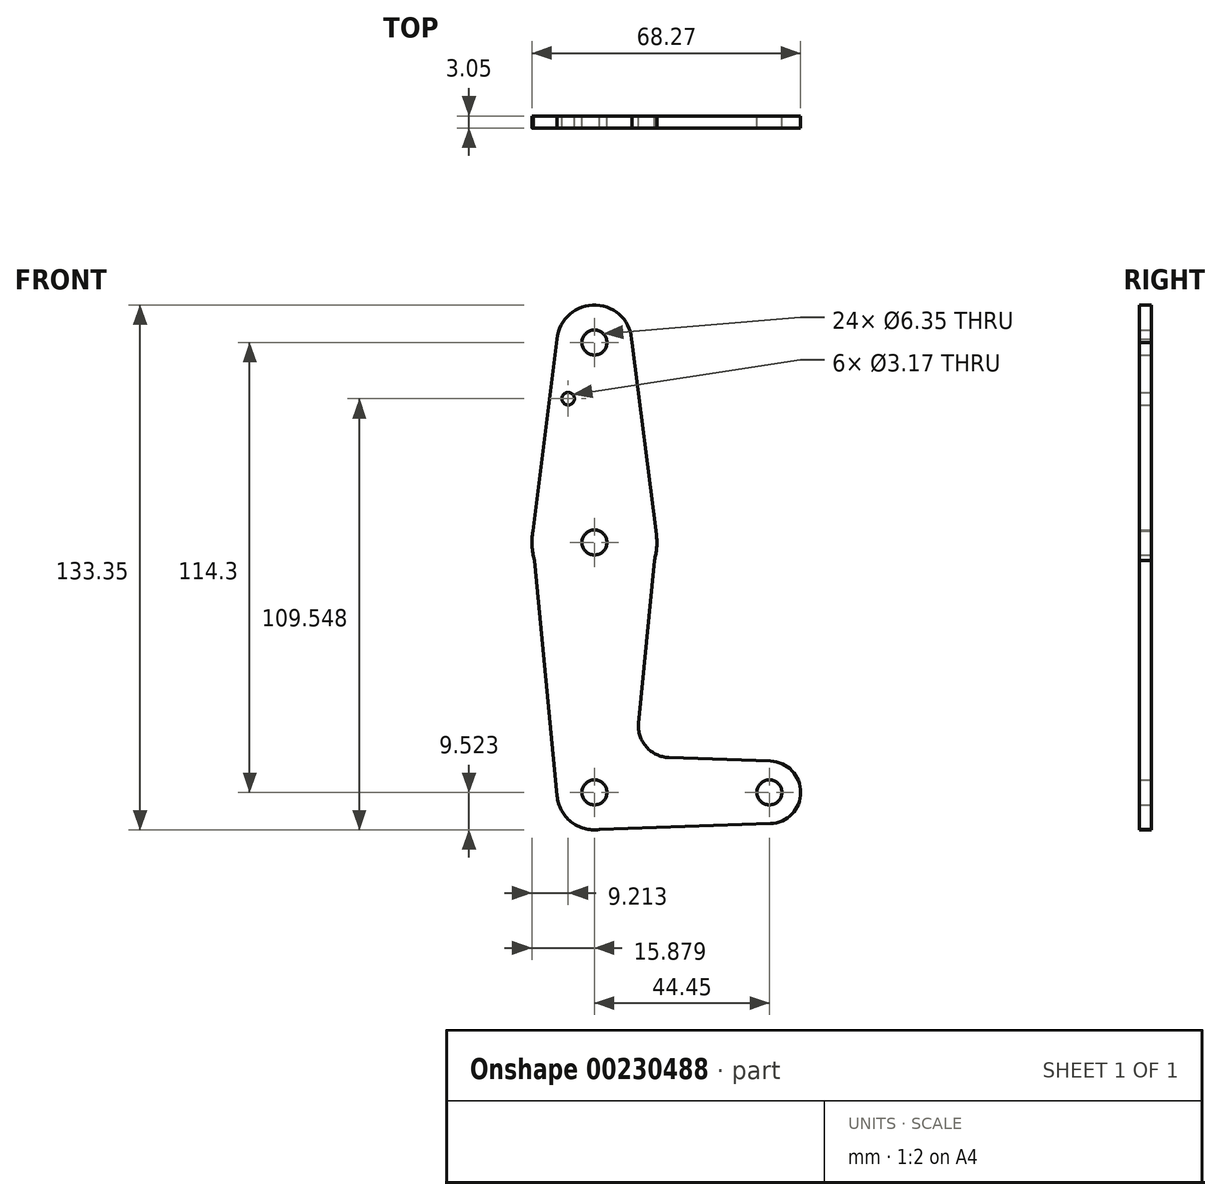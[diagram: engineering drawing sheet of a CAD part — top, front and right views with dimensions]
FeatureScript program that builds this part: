
annotation { "Feature Type Name" : "Feature", "Feature Type Description" : "" }
export const myFeature = defineFeature(function(context is Context, id is Id, definition is map)
    precondition{}
    {
        {
            var Q0;
            Q0=qCreatedBy(makeId("Front.planeOp"),FACE);
            var sketch = newSketch(context, id + "F0", { "sketchPlane" : qUnion([Q0])});
            skLineSegment(sketch, "E0", {"start": v(-22.85, 55.33) * mm, "end": v(-22.85, -58.97) * mm, "construction": true});
            skLineSegment(sketch, "E1", {"start": v(-22.85, -58.97) * mm, "end": v(21.6, -58.97) * mm, "construction": true});
            skCircle(sketch, "E2", {"center": v(-22.85, 55.33) * mm, "radius": 9.53 * mm});
            skCircle(sketch, "E3", {"center": v(-22.85, 4.53) * mm, "radius": 15.88 * mm});
            skCircle(sketch, "E4", {"center": v(-22.85, -58.97) * mm, "radius": 9.53 * mm});
            skCircle(sketch, "E5", {"center": v(21.6, -58.97) * mm, "radius": 7.94 * mm});
            skLineSegment(sketch, "E6", {"start": v(-32.33, 56.22) * mm, "end": v(-38.46, 7.42) * mm});
            skLineSegment(sketch, "E7", {"start": v(-3.98, -50.11) * mm, "end": v(21.88, -51.03) * mm});
            skLineSegment(sketch, "E8", {"start": v(-23.43, -68.47) * mm, "end": v(21.87, -66.9) * mm});
            skLineSegment(sketch, "E9", {"start": v(-7.64, 0) * mm, "end": v(-11.6, -41.41) * mm});
            skCircle(sketch, "E10", {"center": v(-22.85, 55.33) * mm, "radius": 3.18 * mm});
            skCircle(sketch, "E11", {"center": v(-22.85, 4.53) * mm, "radius": 3.18 * mm});
            skCircle(sketch, "E12", {"center": v(-22.85, -58.97) * mm, "radius": 3.18 * mm});
            skCircle(sketch, "E13", {"center": v(21.6, -58.97) * mm, "radius": 3.18 * mm});
            skCircle(sketch, "E14", {"center": v(-29.52, 41.06) * mm, "radius": 1.59 * mm});
            skArc(sketch, "E15.filletArc", {"start": v(-11.6, -41.41) * mm, "mid": v(-9.67, -47.4) * mm, "end": v(-3.98, -50.11) * mm});
            skLineSegment(sketch, "E16", {"start": v(-13.33, 55.33) * mm, "end": v(-7.1, 6.54) * mm});
            skLineSegment(sketch, "E17", {"start": v(-38.06, 0) * mm, "end": v(-32.33, -59.87) * mm});
            skSolve(sketch);
        }
        {
            var Q0;
            Q0 = qSketchRegion(id + "F0", true);
            extrude(context, id + "F1", {"entities" : qUnion([Q0]), "depth" : 3.05 * mm});
        }
    });
